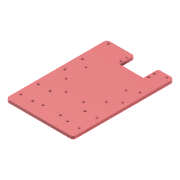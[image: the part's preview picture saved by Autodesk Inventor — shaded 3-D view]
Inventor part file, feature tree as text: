
AUTODESK INVENTOR PART (.ipt)
format: ipt  version: 2022 (Build 260153000, 153)  size: 242,176 bytes
history: native  units: mm
features: sketch x8, hole x7, extrude x2, fillet x2, other x1, projected_geometry x1
ambient origin geometry x8: Origin, YZ Plane, XZ Plane, XY Plane, X Axis, Y Axis, Z Axis, Center Point
bodies: Solid1 (feature_tree)
feature tree (21):
  extrude  "Base"  TaperAngle=0.0deg  [1 undecoded]
  hole  "Bearing Holder Mounting Holes"  [1 undecoded]
  fillet  "Fillet1"  Radius=18.0mm
  hole  "12v Motor Mount Mounting Holes"  [1 undecoded]
  extrude  "Servo Cutout 2"  Depth=10.0mm
  hole  "Servo Mounting Holes 2"  [1 undecoded]
  hole  "Extra Holes For Top Plate"  [1 undecoded]
  hole  "Ultrasonic Sensor Mounting Holes"  [1 undecoded]
  other  "Clearance for Servo"
  hole  "Driver Gear Stopper Mounting Holes"  [1 undecoded]
  fillet  "Fillet2"  Radius=10.0mm
  hole  "CounterBore for Bearing Holder Mounting Holes"  [1 undecoded]
  sketch  "Sketch2"  dims[d2=115.0mm d4=0.0mm]
  sketch  "Sketch5"  dims[d5=20.0mm d6=30.0mm d8=18.0mm]
  sketch  "Sketch8"  dims[d9=3.4mm d10=6.0mm d11=4.0mm d12=2.0mm d13=90.0deg d14=8.0mm d15=20.594885mm d16=10.0mm]
  sketch  "Sketch9"  dims[d18=20.0mm d19=10.0mm]
  sketch  "Sketch10"  dims[d20=50.0mm d21=5.0mm]
  sketch  "Sketch11"  dims[d41=34.0mm d42=69.0mm]
  sketch  "Sketch13"  dims[d43=80.0mm]
  sketch  "Sketch15"  dims[d44=3.2mm d45=6.0mm d46=4.0mm d47=2.0mm d48=90.0deg d49=8.0mm d50=20.594885mm d64=20.0mm d65=40.0mm d67=10.0mm d68=0.0mm d69=0.0mm d70=3.925mm d71=5.0mm d72=3.925mm d73=3.4mm d74=6.0mm d75=4.0mm d76=2.0mm d77=90.0deg d78=8.0mm d79=20.594885mm d84=3.4mm d85=6.0mm d86=4.0mm d87=2.0mm d88=90.0deg d89=6.0mm d90=0.0mm d93=5.0mm d94=50.0mm d95=50.0mm d96=30.0mm d97=8.0mm d98=3.4mm d99=6.0mm d100=7.0mm d101=2.0mm d102=90.0deg d103=6.0mm d104=0.0mm d105=0.5mm d106=0.2mm d108=30.0mm d110=8.0mm d111=50.0mm d123=30.0mm d124=60.5mm d125=3.4mm d126=6.0mm d127=7.0mm d128=2.0mm d129=90.0deg d130=8.0mm d131=20.594885mm d139=7.0mm d140=6.0mm d141=6.0mm d142=2.0mm d143=90.0deg d144=2.0mm d145=0.0mm d146=21.0mm d147=5.0mm d148=3.0mm]
  projected_geometry  "Project Cut Edges1"
note: 8 required parameter values undecoded (feature->parameter linkage not recoverable at this tier; creation-order binding heuristic only, values carry confidence <= 0.55)
